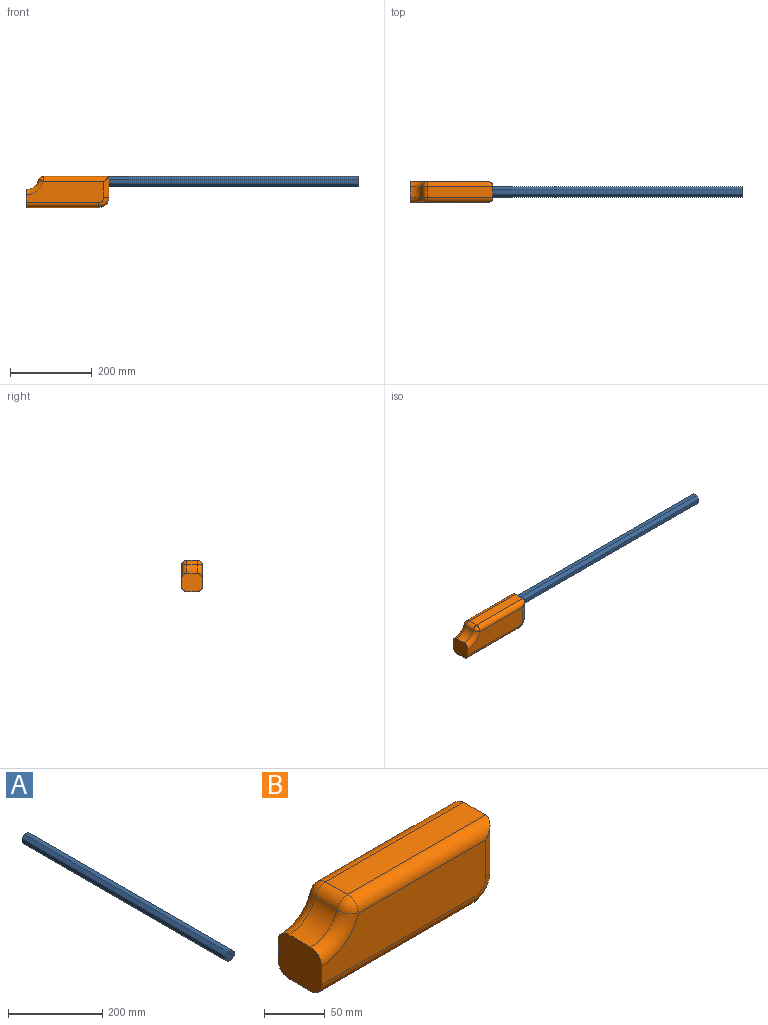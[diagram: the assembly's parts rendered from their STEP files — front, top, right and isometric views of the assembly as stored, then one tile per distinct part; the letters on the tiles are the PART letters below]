
ASSEMBLY  parts=2 mates=1
PART A: 11 faces, bbox 25.4x609.6x25.4 mm
  f0: plane 609.6x7.44mm, normal (0.71,0,0.71), area 6413.6mm2, adj f1,f7,f8,f9
  f1: plane 609.6x10.52mm, normal (0,0,1), area 6413.6mm2, adj f0,f2,f8,f9
  f2: plane 609.6x7.44mm, normal (-0.71,0,0.71), area 6413.6mm2, adj f1,f3,f8,f9
  f3: plane 609.6x10.52mm, normal (-1,0,0), area 6413.6mm2, adj f2,f4,f8,f9
  f4: plane 609.6x7.44mm, normal (-0.71,0,-0.71), area 6413.6mm2, adj f3,f5,f8,f9
  f5: plane 609.6x10.52mm, normal (0,0,-1), area 6413.6mm2, adj f4,f6,f8,f9
  f6: plane 609.6x7.44mm, normal (0.71,0,-0.71), area 6413.6mm2, adj f5,f7,f8,f9
  f7: plane 609.6x10.52mm, normal (1,0,0), area 6413.6mm2, adj f0,f6,f8,f9
  f8: plane 25.4x25.4mm, normal (0,-1,0), area 431.9mm2, adj f0,f1,f2,f3,f4,f5,f6,f7
  f9: plane 25.4x25.4mm, normal (0,1,0), area 431.9mm2, adj f0,f1,f2,f3,f4,f5,f6,f7
  f10: cylinder r=5.71mm len=609.6mm, axis (0,-1,0), area 21889.8mm2, adj f8,f9
PART B: 23 faces, bbox 205.3x50.8x78.3 mm
  f0: plane 160.6x25.4mm, normal (0,0,1), area 4079.3mm2, adj f4,f14,f17,f19
  f1: cylinder r=31.75mm len=30.43mm, axis (0,1,0), area 1033.1mm2, adj f2,f13,f16,f17
  f2: plane 50.8x44.45mm, normal (-1,0,0), area 2119.6mm2, adj f1,f3,f5,f6,f10,f13,f16,f22
  f3: plane 177.8x25.4mm, normal (0,0,-1), area 4516.1mm2, adj f2,f7,f10,f22
  f4: plane 50.8x25.4mm, normal (1,0,0), area 1187.7mm2, adj f0,f7,f8,f12,f20
  f5: plane 190.5x50.8mm, normal (0,-1,0), area 8647.7mm2, adj f2,f16,f19,f20,f21,f22
  f6: plane 190.5x50.8mm, normal (0,1,0), area 8647.7mm2, adj f2,f10,f11,f12,f13,f14
  f7: cylinder r=25.4mm len=25.4mm, axis (0,1,0), area 1013.4mm2, adj f3,f4,f11,f21
  f8: cylinder r=5.71mm len=25.4mm, axis (1,0,0), area 912.1mm2, adj f4,f9
  f9: plane 11.43x11.43mm, normal (1,0,0), area 102.6mm2, adj f8
  f10: cylinder r=12.7mm len=177.8mm, axis (1,0,0), area 3547mm2, adj f2,f3,f6,f11
  f11: torus R=12.7mm, axis (0,-1,0), area 651.3mm2, adj f6,f7,f10,f12
  f12: cylinder r=12.7mm len=50.8mm, axis (0,0,1), area 921.4mm2, adj f4,f6,f11,f14
  f13: torus R=44.45mm, axis (0,-1,0), area 929.3mm2, adj f1,f2,f6,f15
  f14: cylinder r=12.7mm len=160.6mm, axis (-1,0,0), area 3111.8mm2, adj f0,f6,f12,f15
  f15: sphere r=12.7mm, area 206.6mm2, adj f13,f14,f17
  f16: torus R=44.45mm, axis (0,-1,0), area 929.3mm2, adj f1,f2,f5,f18
  f17: cylinder r=12.7mm len=25.4mm, axis (0,1,0), area 413.2mm2, adj f0,f1,f15,f18
  f18: sphere r=12.7mm, area 206.6mm2, adj f16,f17,f19
  f19: cylinder r=12.7mm len=160.6mm, axis (1,0,0), area 3111.8mm2, adj f0,f5,f18,f20
  f20: cylinder r=12.7mm len=50.8mm, axis (0,0,-1), area 921.4mm2, adj f4,f5,f19,f21
  f21: torus R=12.7mm, axis (0,-1,0), area 651.3mm2, adj f5,f7,f20,f22
  f22: cylinder r=12.7mm len=177.8mm, axis (-1,0,0), area 3547mm2, adj f2,f3,f5,f21
PLACE A rot(axis=(0,0,-1),90deg) t=(579.32,-29.49,95.37)mm
PLACE B t=(-233.48,-4.09,31.87)mm fixed
MATE fastened B.f8 <-> A.f10  axis (1,0,0) through (-30.28,-29.49,95.37)mm
